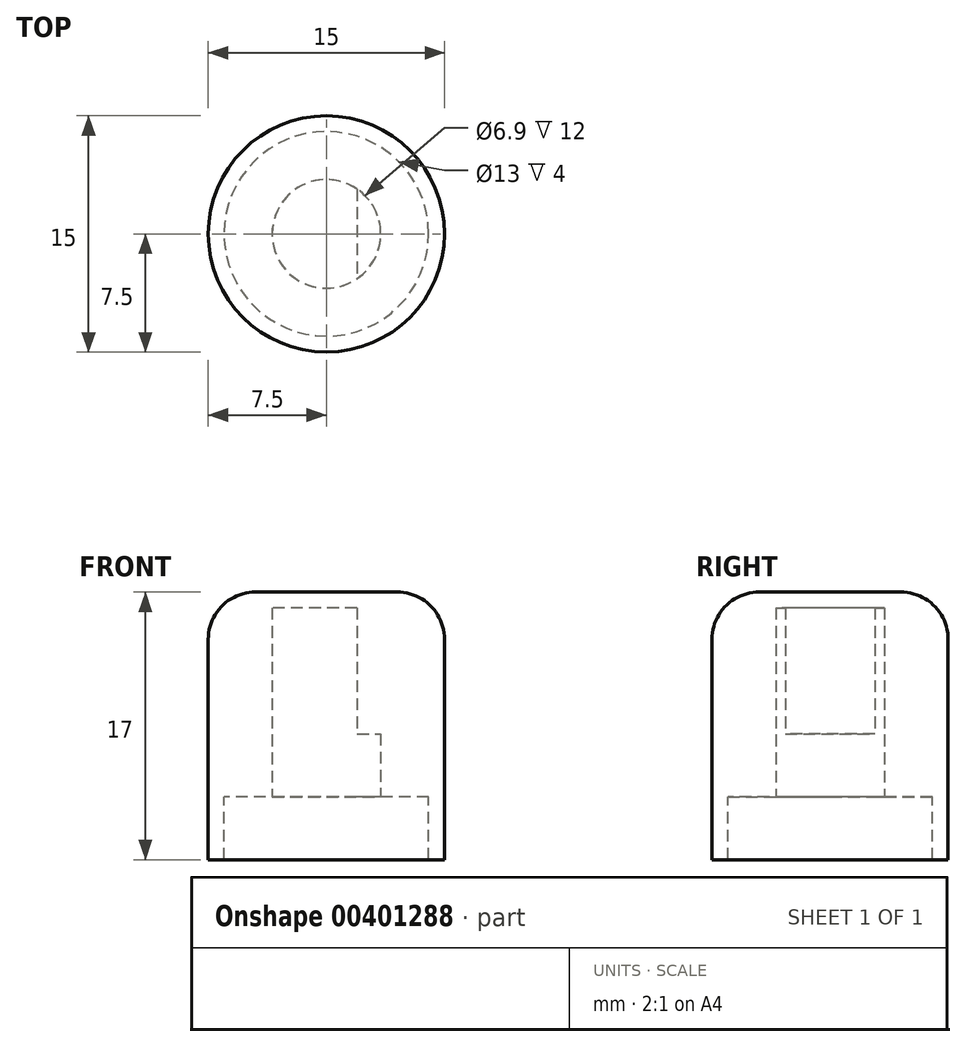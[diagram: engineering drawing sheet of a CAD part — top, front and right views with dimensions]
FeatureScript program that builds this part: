
annotation { "Feature Type Name" : "Feature", "Feature Type Description" : "" }
export const myFeature = defineFeature(function(context is Context, id is Id, definition is map)
    precondition{}
    {
        {
            var Q0;
            Q0=qCreatedBy(makeId("Top.planeOp"),FACE);
            var sketch = newSketch(context, id + "F0", { "sketchPlane" : qUnion([Q0])});
            skCircle(sketch, "E0", {"center": v(0, 0) * mm, "radius": 3.45 * mm});
            skCircle(sketch, "E1", {"center": v(0, 0) * mm, "radius": 7.5 * mm});
            skLineSegment(sketch, "E2", {"start": v(1.95, 2.85) * mm, "end": v(1.95, -2.85) * mm});
            skCircle(sketch, "E3", {"center": v(0, 0) * mm, "radius": 6.5 * mm});
            skSolve(sketch);
        }
        {
            var Q0;
            Q0=makeQuery(id+"F0.imprint","IMPRINT",FACE,{"disambiguationData":[TD([[makeQuery(id+"F0.imprint","IMPRINT",EDGE,{"derivedFrom":sQuery(id+"F0.wireOp",EDGE,"E3")}),1.0]])]});
            var Q1;
            Q1=makeQuery(id+"F0.imprint","IMPRINT",FACE,{"disambiguationData":[TD([[makeQuery(id+"F0.imprint","IMPRINT",EDGE,{"derivedFrom":sQuery(id+"F0.wireOp",EDGE,"E1")}),1.0]])]});
            var Q2;
            {var subQ0=sQuery(id+"F0.wireOp",EDGE,"E2");Q2=makeQuery(id+"F0.imprint","IMPRINT",FACE,{"disambiguationData":[TD([[makeQuery(id+"F0.imprint","IMPRINT",EDGE,{"derivedFrom":subQ0}),-1.0]])]});}
            var Q3;
            {var subQ0=sQuery(id+"F0.wireOp",EDGE,"E2");Q3=makeQuery(id+"F0.imprint","IMPRINT",FACE,{"disambiguationData":[TD([[makeQuery(id+"F0.imprint","IMPRINT",EDGE,{"derivedFrom":subQ0}),1.0]])]});}
            extrude(context, id + "F1", {"entities" : qUnion([Q0, Q1, Q2, Q3]), "depth" : 13 * mm});
        }
        {
            var Q0;
            {var subQ0=sQuery(id+"F0.wireOp",EDGE,"E2");Q0=makeQuery(id+"F0.imprint","IMPRINT",FACE,{"disambiguationData":[TD([[makeQuery(id+"F0.imprint","IMPRINT",EDGE,{"derivedFrom":subQ0}),-1.0]])]});}
            extrude(context, id + "F2", {"entities" : qUnion([Q0]), "operationType" : NewBodyOperationType.REMOVE, "depth" : 12 * mm});
        }
        {
            var Q0;
            {var subQ0=sQuery(id+"F0.wireOp",EDGE,"E2");Q0=makeQuery(id+"F0.imprint","IMPRINT",FACE,{"disambiguationData":[TD([[makeQuery(id+"F0.imprint","IMPRINT",EDGE,{"derivedFrom":subQ0}),1.0]])]});}
            extrude(context, id + "F3", {"entities" : qUnion([Q0]), "operationType" : NewBodyOperationType.REMOVE, "depth" : 4 * mm});
        }
        {
            var Q0;
            Q0=makeQuery(id+"F0.imprint","IMPRINT",FACE,{"disambiguationData":[TD([[makeQuery(id+"F0.imprint","IMPRINT",EDGE,{"derivedFrom":sQuery(id+"F0.wireOp",EDGE,"E1")}),1.0]])]});
            extrude(context, id + "F4", {"entities" : qUnion([Q0]), "operationType" : NewBodyOperationType.ADD, "oppositeDirection" : true, "depth" : 4 * mm});
        }
        {
            var Q0;
            Q0=makeQuery(id+"F1.opExtrude","CAP_EDGE",EDGE,{"disambiguationData":[OSD([sQuery(id+"F0.wireOp",EDGE,"E1")])],"isStart":false});
            fillet(context, id + "F5", {"entities" : qUnion([Q0]), "radius" : 3 * mm, "tangentPropagation" : true, "allowEdgeOverflow" : false});
        }
    });
